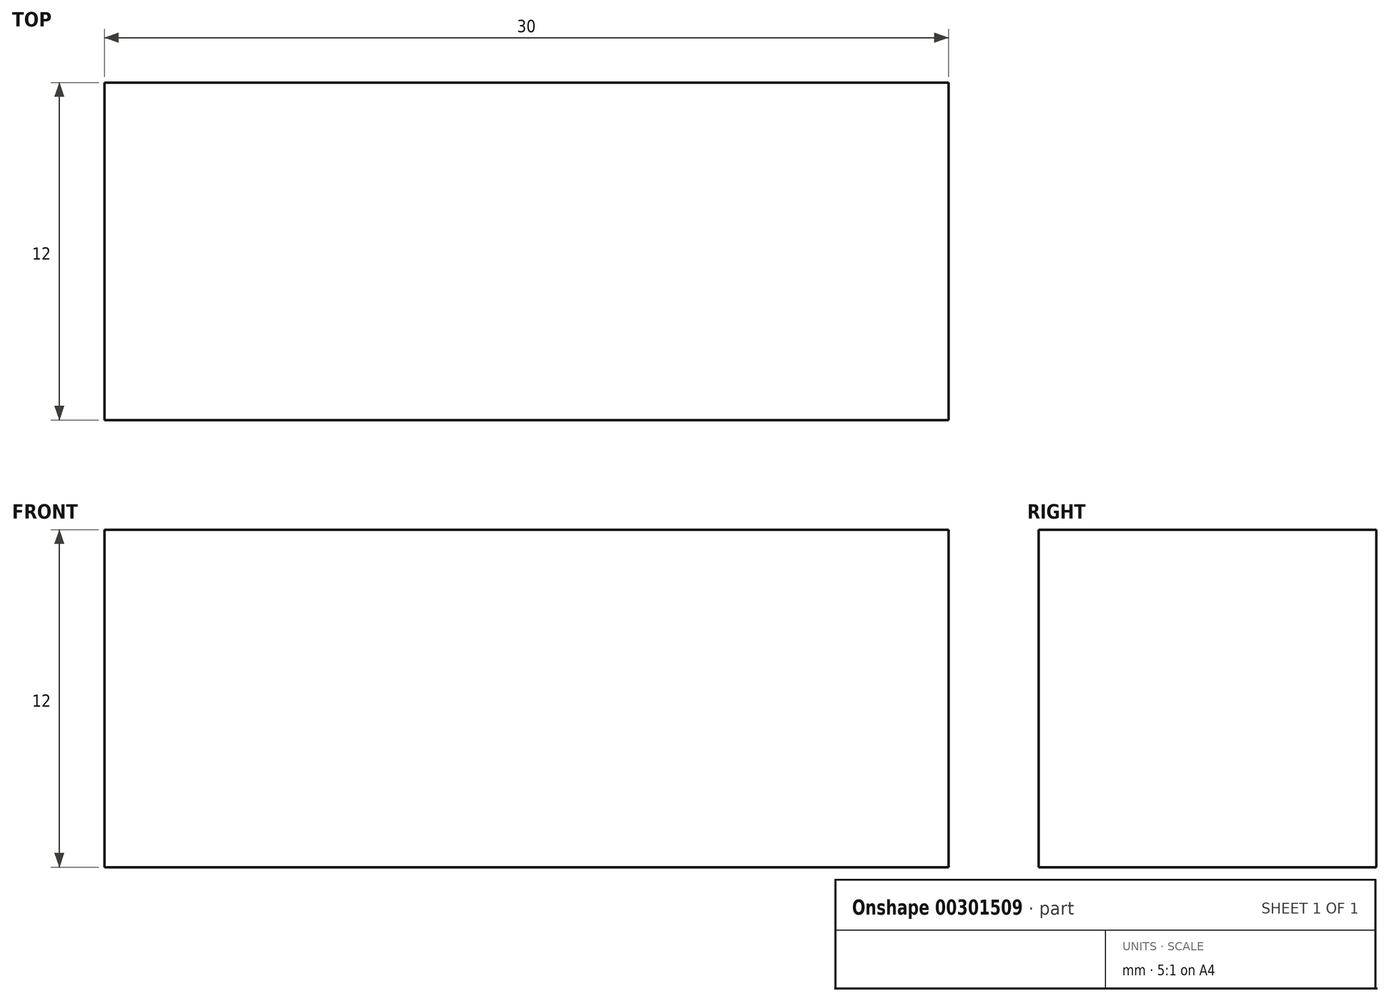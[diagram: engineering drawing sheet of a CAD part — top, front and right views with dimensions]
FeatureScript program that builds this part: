
annotation { "Feature Type Name" : "Feature", "Feature Type Description" : "" }
export const myFeature = defineFeature(function(context is Context, id is Id, definition is map)
    precondition{}
    {
        {
            var Q0;
            Q0=qCreatedBy(makeId("Front.planeOp"),FACE);
            var sketch = newSketch(context, id + "F0", { "sketchPlane" : qUnion([Q0])});
            skLineSegment(sketch, "E0.bottom", {"start": v(0, 0) * mm, "end": v(30, 0) * mm});
            skLineSegment(sketch, "E0.top", {"start": v(0, 12) * mm, "end": v(30, 12) * mm});
            skLineSegment(sketch, "E0.left", {"start": v(0, 0) * mm, "end": v(0, 12) * mm});
            skLineSegment(sketch, "E0.right", {"start": v(30, 0) * mm, "end": v(30, 12) * mm});
            skSolve(sketch);
        }
        {
            var Q0;
            Q0=qSketchRegion(id+"F0",true);
            extrude(context, id + "F1", {"entities" : qUnion([Q0]), "depth" : 12 * mm});
        }
    });
